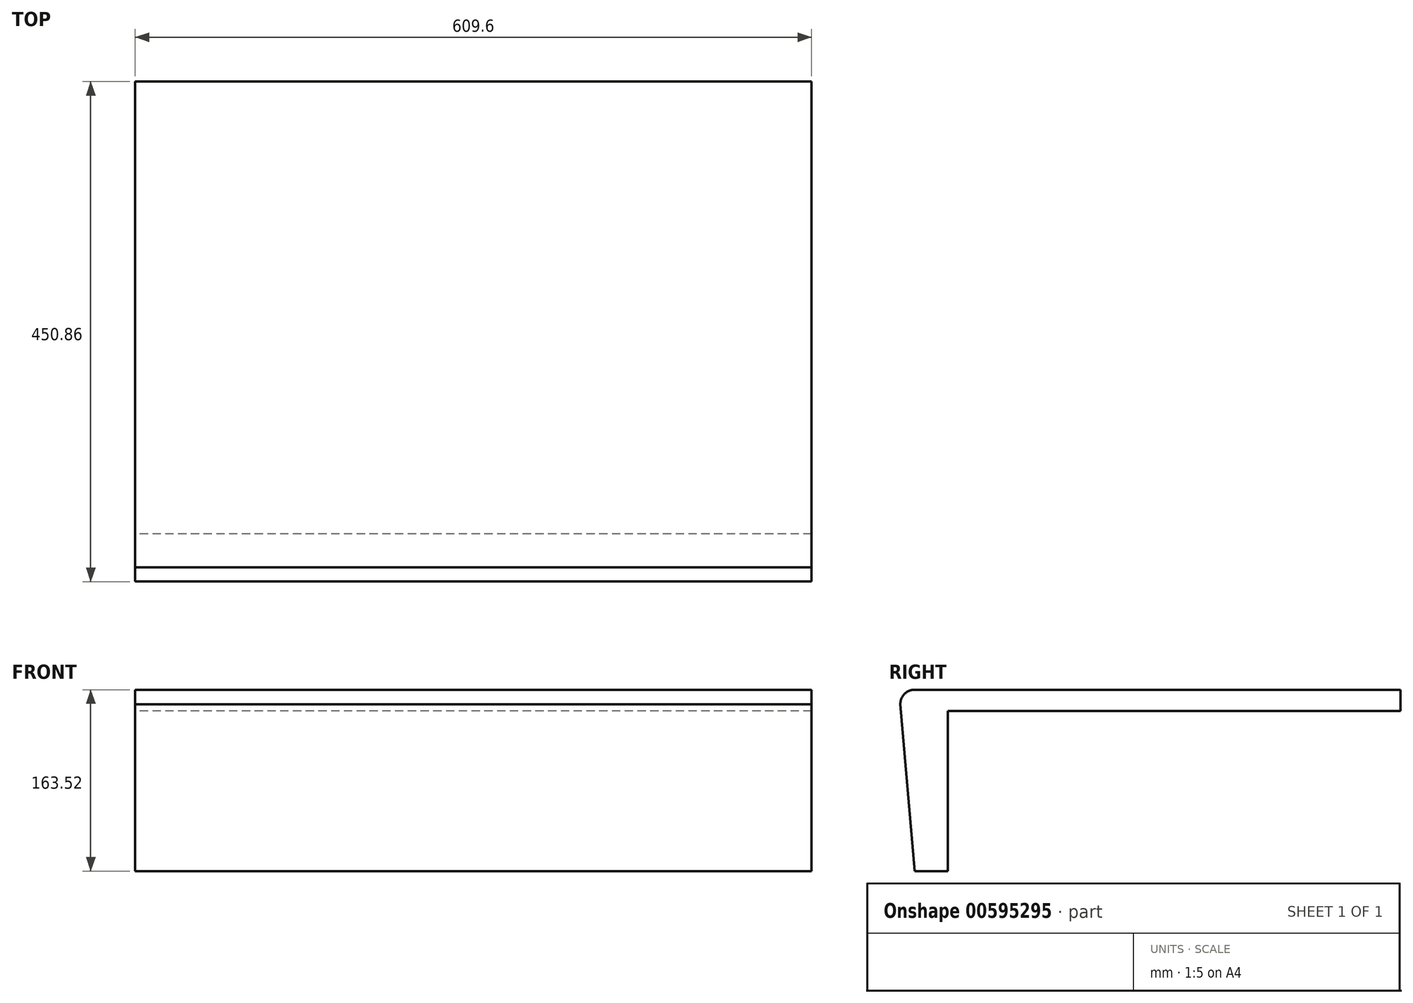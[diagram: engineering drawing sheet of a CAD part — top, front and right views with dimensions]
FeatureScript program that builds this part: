
annotation { "Feature Type Name" : "Feature", "Feature Type Description" : "" }
export const myFeature = defineFeature(function(context is Context, id is Id, definition is map)
    precondition{}
    {
        {
            var Q0;
            Q0=qCreatedBy(makeId("Right.planeOp"),FACE);
            var sketch = newSketch(context, id + "F0", { "sketchPlane" : qUnion([Q0])});
            skLineSegment(sketch, "E0", {"start": v(-143.8, 55.02) * mm, "end": v(264.18, 55.02) * mm});
            skLineSegment(sketch, "E1", {"start": v(-173.74, -89.44) * mm, "end": v(-186.67, 60.84) * mm});
            skLineSegment(sketch, "E2", {"start": v(-173.67, 74.07) * mm, "end": v(264.18, 74.07) * mm});
            skLineSegment(sketch, "E3", {"start": v(264.18, 74.07) * mm, "end": v(264.18, 55.02) * mm});
            skArc(sketch, "E4", {"start": v(-173.67, 74.07) * mm, "mid": v(-183.04, 70.28) * mm, "end": v(-186.67, 60.84) * mm});
            skPoint(sketch, "E4.first.point", {"position": v(-186.67, 60.84) * mm});
            skPoint(sketch, "E4.second.point", {"position": v(-173.67, 74.07) * mm});
            skPoint(sketch, "E4.third.point", {"position": v(-168.14, 50.1) * mm});
            skLineSegment(sketch, "E5", {"start": v(-143.8, 55.02) * mm, "end": v(-143.8, -89.44) * mm});
            skLineSegment(sketch, "E6", {"start": v(-143.8, -89.44) * mm, "end": v(-173.74, -89.44) * mm});
            skSolve(sketch);
        }
        {
            var Q0;
            Q0=makeQuery(id+"F0.imprint","IMPRINT",FACE,{"disambiguationData":[TD([[makeQuery(id+"F0.imprint","IMPRINT",EDGE,{"derivedFrom":sQuery(id+"F0.wireOp",EDGE,"E0")}),1.0]])]});
            extrude(context, id + "F1", {"entities" : qUnion([Q0]), "depth" : 609.6 * mm, "offsetDistance" : 25.4 * mm});
        }
    });
